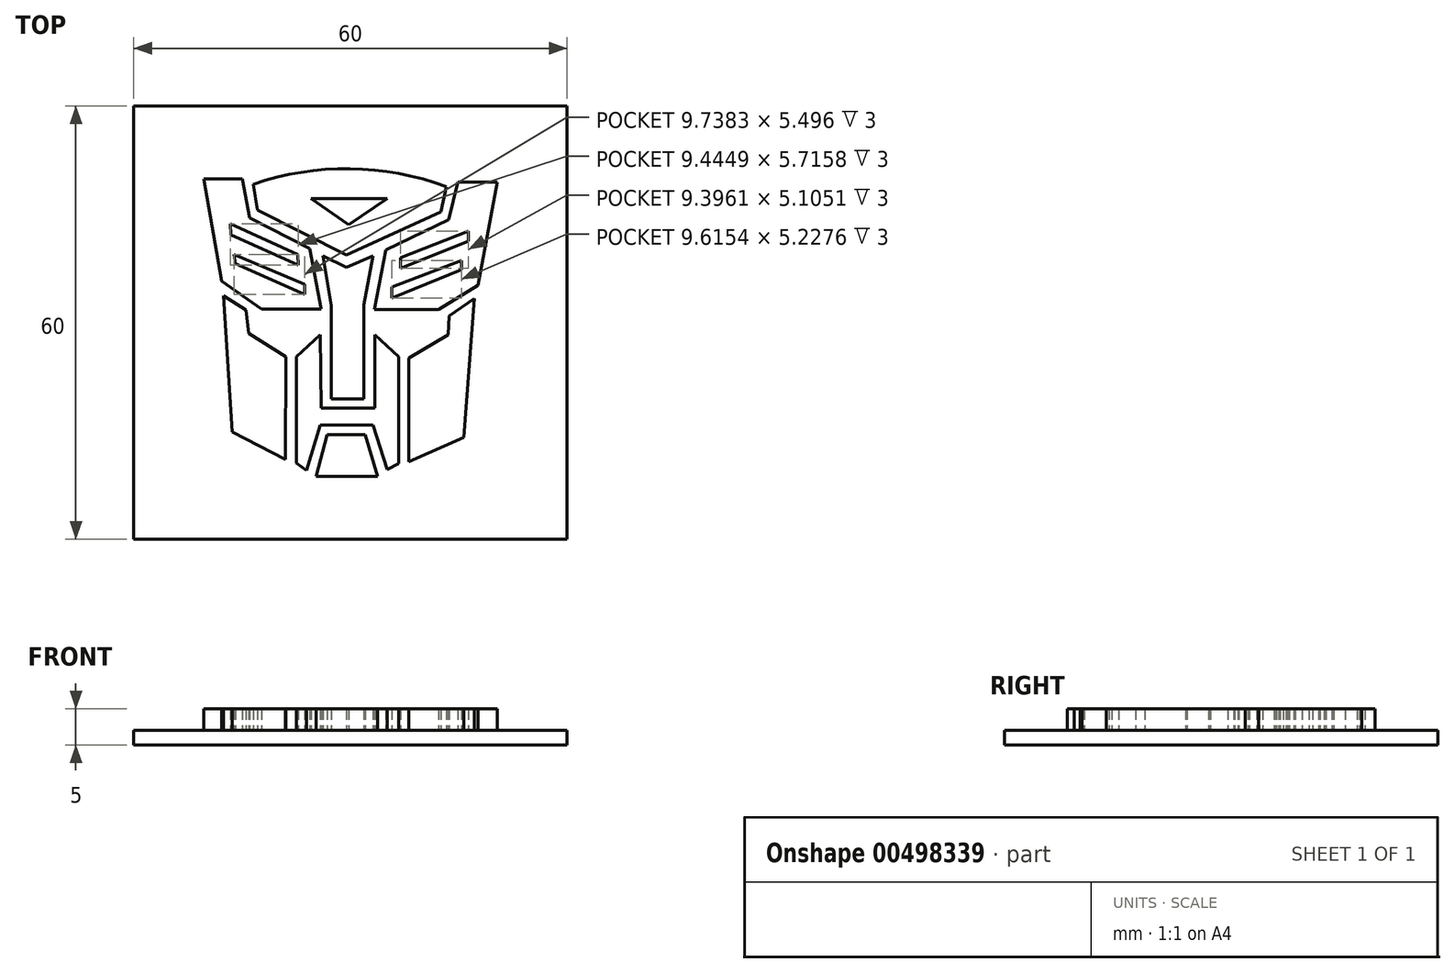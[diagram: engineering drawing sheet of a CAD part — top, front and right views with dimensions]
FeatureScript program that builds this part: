
annotation { "Feature Type Name" : "Feature", "Feature Type Description" : "" }
export const myFeature = defineFeature(function(context is Context, id is Id, definition is map)
    precondition{}
    {
        {
            var Q0;
            Q0=qCreatedBy(makeId("Top.planeOp"),FACE);
            var sketch = newSketch(context, id + "F0", { "sketchPlane" : qUnion([Q0])});
            skLineSegment(sketch, "E0", {"start": v(-4.73, -21.33) * mm, "end": v(3.73, -21.33) * mm});
            skLineSegment(sketch, "E1", {"start": v(3.73, -21.33) * mm, "end": v(2.05, -15.55) * mm});
            skLineSegment(sketch, "E2", {"start": v(2.05, -15.55) * mm, "end": v(-3.26, -15.55) * mm});
            skLineSegment(sketch, "E3", {"start": v(-3.26, -15.55) * mm, "end": v(-4.73, -21.33) * mm});
            skLineSegment(sketch, "E4", {"start": v(-7.5, -19.45) * mm, "end": v(-6.08, -20.45) * mm});
            skLineSegment(sketch, "E5", {"start": v(-6.08, -20.45) * mm, "end": v(-4.2, -14.2) * mm});
            skLineSegment(sketch, "E6", {"start": v(-4.2, -14.2) * mm, "end": v(3.12, -14.2) * mm});
            skLineSegment(sketch, "E7", {"start": v(3.12, -14.2) * mm, "end": v(5.06, -20.38) * mm});
            skLineSegment(sketch, "E8", {"start": v(5.06, -20.38) * mm, "end": v(6.68, -19.5) * mm});
            skLineSegment(sketch, "E9", {"start": v(6.68, -19.5) * mm, "end": v(6.68, -4.74) * mm});
            skLineSegment(sketch, "E10", {"start": v(6.68, -4.74) * mm, "end": v(3.4, -1.71) * mm});
            skLineSegment(sketch, "E11", {"start": v(3.4, -1.71) * mm, "end": v(3.4, -11.85) * mm});
            skLineSegment(sketch, "E12", {"start": v(3.4, -11.85) * mm, "end": v(-4.06, -11.85) * mm});
            skLineSegment(sketch, "E13", {"start": v(-4.06, -11.85) * mm, "end": v(-4.2, -1.71) * mm});
            skLineSegment(sketch, "E14", {"start": v(-4.2, -1.71) * mm, "end": v(-7.5, -4.74) * mm});
            skLineSegment(sketch, "E15", {"start": v(-7.5, -4.74) * mm, "end": v(-7.5, -19.45) * mm});
            skLineSegment(sketch, "E16", {"start": v(-0.23, 13.53) * mm, "end": v(5.08, 17.16) * mm});
            skLineSegment(sketch, "E17", {"start": v(5.08, 17.16) * mm, "end": v(-5.47, 17.16) * mm});
            skLineSegment(sketch, "E18", {"start": v(-5.47, 17.16) * mm, "end": v(-0.23, 13.53) * mm});
            skLineSegment(sketch, "E19", {"start": v(-5.61, 10.23) * mm, "end": v(-13.94, 14.53) * mm});
            skLineSegment(sketch, "E20", {"start": v(-13.94, 14.53) * mm, "end": v(-15.01, 19.9) * mm});
            skLineSegment(sketch, "E21", {"start": v(-15.01, 19.9) * mm, "end": v(-20.33, 19.9) * mm});
            skLineSegment(sketch, "E22", {"start": v(-20.33, 19.9) * mm, "end": v(-17.85, 5.74) * mm});
            skLineSegment(sketch, "E23", {"start": v(-17.85, 5.74) * mm, "end": v(-12.32, 1.9) * mm});
            skLineSegment(sketch, "E24", {"start": v(-12.32, 1.9) * mm, "end": v(-4.06, 1.9) * mm});
            skLineSegment(sketch, "E25", {"start": v(-4.06, 1.9) * mm, "end": v(-5.61, 10.23) * mm});
            skLineSegment(sketch, "E26", {"start": v(-2.66, 2.32) * mm, "end": v(-2.66, -10.58) * mm});
            skLineSegment(sketch, "E27", {"start": v(-2.66, -10.58) * mm, "end": v(1.85, -10.58) * mm});
            skLineSegment(sketch, "E28", {"start": v(1.85, -10.58) * mm, "end": v(1.85, 2.45) * mm});
            skLineSegment(sketch, "E29", {"start": v(1.85, 2.45) * mm, "end": v(3.12, 9.23) * mm});
            skLineSegment(sketch, "E30", {"start": v(3.12, 9.23) * mm, "end": v(-0.57, 7.68) * mm});
            skLineSegment(sketch, "E31", {"start": v(-0.57, 7.68) * mm, "end": v(-3.8, 9.23) * mm});
            skLineSegment(sketch, "E32", {"start": v(-3.8, 9.23) * mm, "end": v(-2.66, 2.32) * mm});
            skLineSegment(sketch, "E33", {"start": v(-6.36, 5.33) * mm, "end": v(-16.1, 9.42) * mm});
            skLineSegment(sketch, "E34", {"start": v(-16.1, 9.42) * mm, "end": v(-15.95, 8.2) * mm});
            skLineSegment(sketch, "E35", {"start": v(-15.95, 8.2) * mm, "end": v(-6.36, 3.93) * mm});
            skLineSegment(sketch, "E36", {"start": v(-6.36, 3.93) * mm, "end": v(-6.36, 5.33) * mm});
            skLineSegment(sketch, "E37", {"start": v(13.28, 18.83) * mm, "end": v(12.53, 15.35) * mm});
            skArc(sketch, "E38", {"start": v(13.28, 18.83) * mm, "mid": v(-0.06, 21.31) * mm, "end": v(-13.46, 19.17) * mm});
            skLineSegment(sketch, "E39", {"start": v(12.53, 15.35) * mm, "end": v(-0.57, 9.36) * mm});
            skLineSegment(sketch, "E40", {"start": v(-0.57, 9.36) * mm, "end": v(-12.86, 15.6) * mm});
            skLineSegment(sketch, "E41", {"start": v(-12.86, 15.6) * mm, "end": v(-13.46, 19.17) * mm});
            skLineSegment(sketch, "E42", {"start": v(-7.29, 9.42) * mm, "end": v(-16.66, 13.66) * mm});
            skLineSegment(sketch, "E43", {"start": v(-16.66, 13.66) * mm, "end": v(-16.54, 12.15) * mm});
            skLineSegment(sketch, "E44", {"start": v(-16.54, 12.15) * mm, "end": v(-7.22, 7.95) * mm});
            skLineSegment(sketch, "E45", {"start": v(-7.22, 7.95) * mm, "end": v(-7.29, 9.42) * mm});
            skLineSegment(sketch, "E46", {"start": v(13.67, 0.9) * mm, "end": v(13.53, -1.65) * mm});
            skLineSegment(sketch, "E47", {"start": v(13.53, -1.65) * mm, "end": v(8.1, -4.94) * mm});
            skLineSegment(sketch, "E48", {"start": v(8.1, -4.94) * mm, "end": v(8.1, -19.24) * mm});
            skLineSegment(sketch, "E49", {"start": v(8.1, -19.24) * mm, "end": v(15.7, -15.9) * mm});
            skLineSegment(sketch, "E50", {"start": v(15.7, -15.9) * mm, "end": v(17.16, 3.32) * mm});
            skLineSegment(sketch, "E51", {"start": v(17.16, 3.32) * mm, "end": v(13.67, 0.9) * mm});
            skLineSegment(sketch, "E52", {"start": v(16.35, 11.24) * mm, "end": v(16.35, 12.66) * mm});
            skLineSegment(sketch, "E53", {"start": v(16.35, 12.66) * mm, "end": v(6.96, 8.96) * mm});
            skLineSegment(sketch, "E54", {"start": v(6.96, 8.96) * mm, "end": v(6.96, 7.56) * mm});
            skLineSegment(sketch, "E55", {"start": v(6.96, 7.56) * mm, "end": v(16.35, 11.24) * mm});
            skLineSegment(sketch, "E56", {"start": v(15.35, 7.35) * mm, "end": v(15.35, 8.62) * mm});
            skLineSegment(sketch, "E57", {"start": v(15.35, 8.62) * mm, "end": v(5.74, 4.93) * mm});
            skLineSegment(sketch, "E58", {"start": v(5.74, 4.93) * mm, "end": v(5.74, 3.4) * mm});
            skLineSegment(sketch, "E59", {"start": v(5.74, 3.4) * mm, "end": v(15.35, 7.35) * mm});
            skLineSegment(sketch, "E60", {"start": v(14.89, 19.44) * mm, "end": v(13.6, 14.27) * mm});
            skLineSegment(sketch, "E61", {"start": v(13.6, 14.27) * mm, "end": v(4.87, 10.04) * mm});
            skLineSegment(sketch, "E62", {"start": v(3.33, 1.78) * mm, "end": v(12.2, 1.78) * mm});
            skLineSegment(sketch, "E63", {"start": v(12.2, 1.78) * mm, "end": v(17.64, 5.2) * mm});
            skLineSegment(sketch, "E64", {"start": v(17.64, 5.2) * mm, "end": v(20.33, 19.44) * mm});
            skLineSegment(sketch, "E65", {"start": v(20.33, 19.44) * mm, "end": v(14.89, 19.44) * mm});
            skLineSegment(sketch, "E66", {"start": v(-14.49, 1.77) * mm, "end": v(-17.56, 3.72) * mm});
            skLineSegment(sketch, "E67", {"start": v(-17.56, 3.72) * mm, "end": v(-16.37, -15.15) * mm});
            skLineSegment(sketch, "E68", {"start": v(-16.37, -15.15) * mm, "end": v(-9.04, -18.97) * mm});
            skLineSegment(sketch, "E69", {"start": v(-9.04, -18.97) * mm, "end": v(-8.96, -4.74) * mm});
            skLineSegment(sketch, "E70", {"start": v(-8.96, -4.74) * mm, "end": v(-14.07, -1.52) * mm});
            skLineSegment(sketch, "E71", {"start": v(-14.07, -1.52) * mm, "end": v(-14.49, 1.77) * mm});
            skLineSegment(sketch, "E72", {"start": v(-24.88, 24.88) * mm, "end": v(-24.88, -24.88) * mm});
            skLineSegment(sketch, "E73", {"start": v(-24.88, -24.88) * mm, "end": v(24.88, -24.88) * mm});
            skLineSegment(sketch, "E74", {"start": v(24.88, -24.88) * mm, "end": v(24.88, 24.88) * mm});
            skLineSegment(sketch, "E75", {"start": v(24.88, 24.88) * mm, "end": v(-24.88, 24.88) * mm});
            skLineSegment(sketch, "E76", {"start": v(4.87, 10.04) * mm, "end": v(3.33, 1.78) * mm});
            skSolve(sketch);
        }
        {
            var Q0;
            Q0=qCreatedBy(makeId("Top.planeOp"),FACE);
            var sketch = newSketch(context, id + "F1", { "sketchPlane" : qUnion([Q0])});
            skLineSegment(sketch, "E77.bottom", {"start": v(30, 30) * mm, "end": v(-30, 30) * mm});
            skLineSegment(sketch, "E77.top", {"start": v(30, -30) * mm, "end": v(-30, -30) * mm});
            skLineSegment(sketch, "E77.left", {"start": v(30, 30) * mm, "end": v(30, -30) * mm});
            skLineSegment(sketch, "E77.right", {"start": v(-30, 30) * mm, "end": v(-30, -30) * mm});
            skPoint(sketch, "E77.middle", {"position": v(0, 0) * mm});
            skSolve(sketch);
        }
        {
            var Q0;
            Q0=makeQuery(id+"F0.imprint","IMPRINT",FACE,{"disambiguationData":[TD([[makeQuery(id+"F0.imprint","IMPRINT",EDGE,{"derivedFrom":sQuery(id+"F0.wireOp",EDGE,"E16")}),-1.0]])]});
            var Q1;
            Q1=makeQuery(id+"F0.imprint","IMPRINT",FACE,{"disambiguationData":[TD([[makeQuery(id+"F0.imprint","IMPRINT",EDGE,{"derivedFrom":sQuery(id+"F0.wireOp",EDGE,"E52")}),-1.0]])]});
            var Q2;
            Q2=makeQuery(id+"F0.imprint","IMPRINT",FACE,{"disambiguationData":[TD([[makeQuery(id+"F0.imprint","IMPRINT",EDGE,{"derivedFrom":sQuery(id+"F0.wireOp",EDGE,"E19")}),1.0]])]});
            var Q3;
            Q3=makeQuery(id+"F0.imprint","IMPRINT",FACE,{"disambiguationData":[TD([[makeQuery(id+"F0.imprint","IMPRINT",EDGE,{"derivedFrom":sQuery(id+"F0.wireOp",EDGE,"E66")}),1.0]])]});
            var Q4;
            Q4=makeQuery(id+"F0.imprint","IMPRINT",FACE,{"disambiguationData":[TD([[makeQuery(id+"F0.imprint","IMPRINT",EDGE,{"derivedFrom":sQuery(id+"F0.wireOp",EDGE,"E46")}),1.0]])]});
            var Q5;
            Q5=makeQuery(id+"F0.imprint","IMPRINT",FACE,{"disambiguationData":[TD([[makeQuery(id+"F0.imprint","IMPRINT",EDGE,{"derivedFrom":sQuery(id+"F0.wireOp",EDGE,"E26")}),1.0]])]});
            var Q6;
            Q6=makeQuery(id+"F0.imprint","IMPRINT",FACE,{"disambiguationData":[TD([[makeQuery(id+"F0.imprint","IMPRINT",EDGE,{"derivedFrom":sQuery(id+"F0.wireOp",EDGE,"E4")}),1.0]])]});
            var Q7;
            Q7=makeQuery(id+"F0.imprint","IMPRINT",FACE,{"disambiguationData":[TD([[makeQuery(id+"F0.imprint","IMPRINT",EDGE,{"derivedFrom":sQuery(id+"F0.wireOp",EDGE,"E0")}),1.0]])]});
            extrude(context, id + "F2", {"entities" : qUnion([Q0, Q1, Q2, Q3, Q4, Q5, Q6, Q7]), "depth" : 5 * mm});
        }
        {
            var Q0;
            Q0=makeQuery(id+"F1.imprint","IMPRINT",FACE,{"disambiguationData":[TD([[makeQuery(id+"F1.imprint","IMPRINT",EDGE,{"derivedFrom":sQuery(id+"F1.wireOp",EDGE,"E77.bottom")}),1.0]])]});
            extrude(context, id + "F3", {"entities" : qUnion([Q0]), "operationType" : NewBodyOperationType.ADD, "depth" : 2 * mm});
        }
    });
